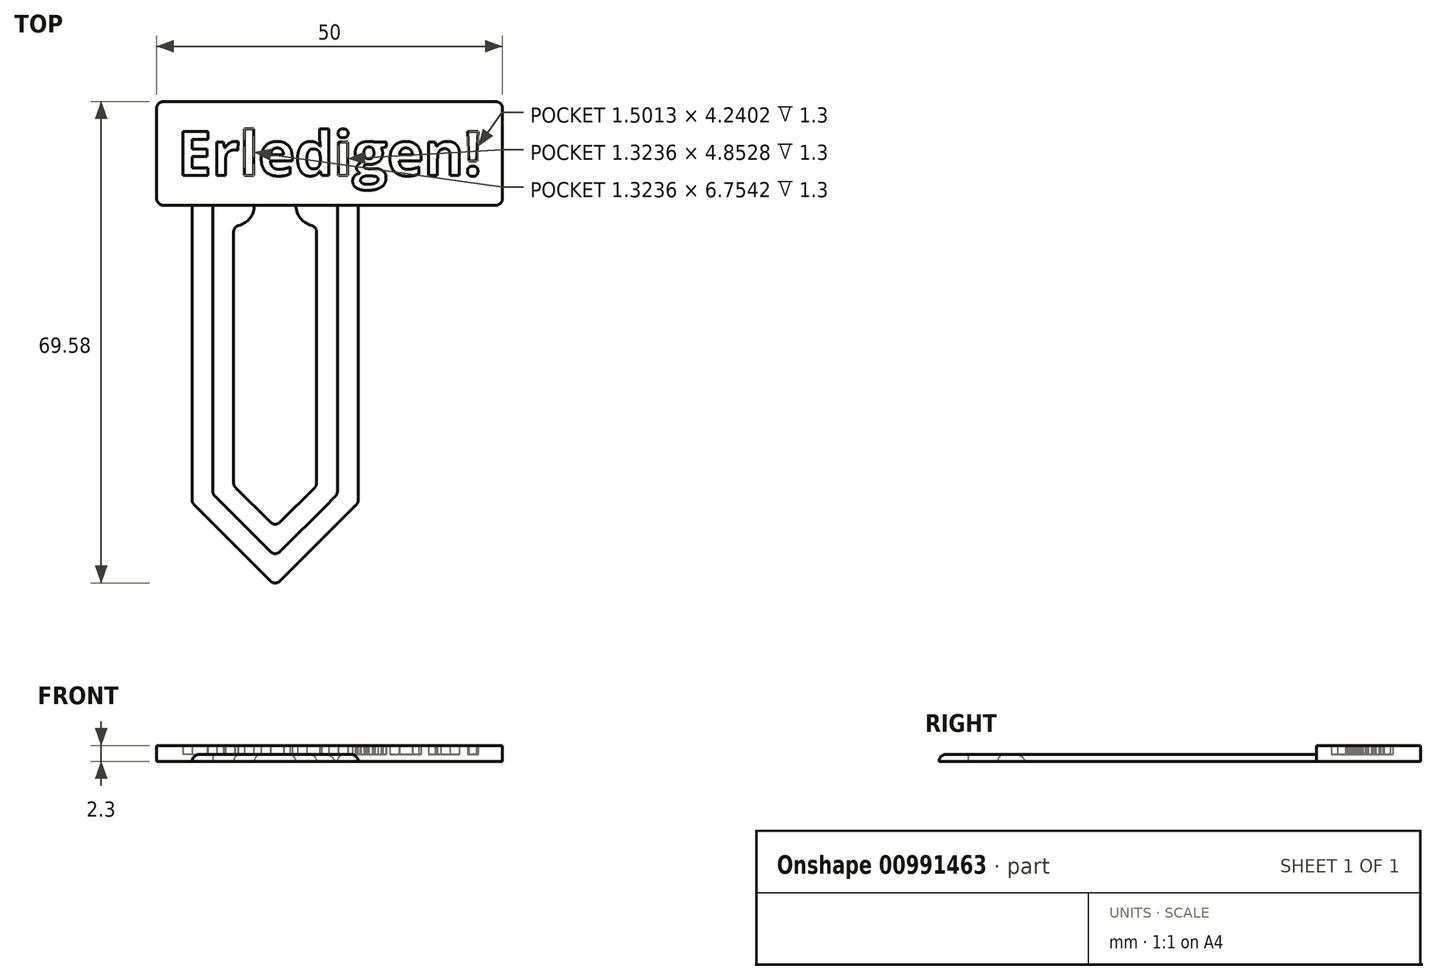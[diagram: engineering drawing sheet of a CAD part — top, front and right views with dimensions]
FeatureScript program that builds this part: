
annotation { "Feature Type Name" : "Feature", "Feature Type Description" : "" }
export const myFeature = defineFeature(function(context is Context, id is Id, definition is map)
    precondition{}
    {
        {
            var Q0;
            Q0=qCreatedBy(makeId("Top.planeOp"),FACE);
            var sketch = newSketch(context, id + "F0", { "sketchPlane" : qUnion([Q0])});
            skLineSegment(sketch, "E0", {"start": v(-14.18, 18.01) * mm, "end": v(-14.18, -24.99) * mm});
            skLineSegment(sketch, "E1", {"start": v(-11.18, 18.01) * mm, "end": v(-11.18, -23.75) * mm});
            skLineSegment(sketch, "E2", {"start": v(-8.18, 15.01) * mm, "end": v(-8.18, -22.5) * mm});
            skLineSegment(sketch, "E3", {"start": v(-2.18, 18.01) * mm, "end": v(-2.18, -9.23) * mm, "construction": true});
            skLineSegment(sketch, "E4", {"start": v(-8.18, -22.5) * mm, "end": v(-2.18, -28.5) * mm});
            skLineSegment(sketch, "E5", {"start": v(-11.18, -23.75) * mm, "end": v(-2.18, -32.75) * mm});
            skLineSegment(sketch, "E6", {"start": v(-2.18, -36.99) * mm, "end": v(-14.18, -24.99) * mm});
            skLineSegment(sketch, "E7.MirrorCS", {"start": v(9.82, 18.01) * mm, "end": v(9.82, -24.99) * mm});
            skLineSegment(sketch, "E8.MirrorCS", {"start": v(6.82, 18.01) * mm, "end": v(6.82, -23.75) * mm});
            skLineSegment(sketch, "E9.MirrorCS", {"start": v(3.82, -22.5) * mm, "end": v(-2.18, -28.5) * mm});
            skLineSegment(sketch, "E10.MirrorCS", {"start": v(6.82, -23.75) * mm, "end": v(-2.18, -32.75) * mm});
            skLineSegment(sketch, "E11.MirrorCS", {"start": v(3.82, 15.01) * mm, "end": v(3.82, -22.5) * mm});
            skLineSegment(sketch, "E12.MirrorCS", {"start": v(-2.18, -36.99) * mm, "end": v(9.82, -24.99) * mm});
            skLineSegment(sketch, "E13.bottom", {"start": v(30.68, 18.01) * mm, "end": v(-19.32, 18.01) * mm});
            skLineSegment(sketch, "E13.top", {"start": v(30.68, 33.01) * mm, "end": v(-19.32, 33.01) * mm});
            skLineSegment(sketch, "E13.left", {"start": v(30.68, 18.01) * mm, "end": v(30.68, 33.01) * mm});
            skLineSegment(sketch, "E13.right", {"start": v(-19.32, 18.01) * mm, "end": v(-19.32, 33.01) * mm});
            skArc(sketch, "E14", {"start": v(-5.18, 18.01) * mm, "mid": v(-6.06, 15.9) * mm, "end": v(-8.18, 15.01) * mm});
            skArc(sketch, "E15", {"start": v(0.82, 18.01) * mm, "mid": v(1.7, 15.9) * mm, "end": v(3.82, 15.01) * mm});
            skText(sketch, "E16", { "text": "Erledigen!", "fontName": "OpenSans-Bold.ttf"});
            skLineSegment(sketch, "E17", {"start": v(5.68, 33.01) * mm, "end": v(5.68, 18.01) * mm, "construction": true});
            skLineSegment(sketch, "E18", {"start": v(-19.32, 25.51) * mm, "end": v(30.68, 25.51) * mm, "construction": true});
            const initialGuessF0  = {"E16": [-0.01632, 0.02231, 1, 0, 0.0064]};
            skSetInitialGuess(sketch, initialGuessF0);
            skSolve(sketch);
        }
        {
            var Q0;
            {var subQ1=sQuery(id+"F0.wireOp",EDGE,"E0");Q0=makeQuery(id+"F0.imprint","IMPRINT",FACE,{"disambiguationData":[TD([[makeQuery(id+"F0.imprint","IMPRINT",EDGE,{"derivedFrom":subQ1}),1.0]])]});}
            var Q1;
            Q1=makeQuery(id+"F0.imprint","IMPRINT",FACE,{"disambiguationData":[TD([[makeQuery(id+"F0.imprint","IMPRINT",EDGE,{"derivedFrom":sQuery(id+"F0.wireOp",EDGE,"E2")}),1.0]])]});
            var Q2;
            Q2=makeQuery(id+"F0.imprint","IMPRINT",FACE,{"disambiguationData":[TD([[makeQuery(id+"F0.imprint","IMPRINT",EDGE,{"derivedFrom":sQuery(id+"F0.wireOp",EDGE,"E16.sketch_text.stroke-0")}),-1.0]])]});
            var Q3;
            Q3=makeQuery(id+"F0.imprint","IMPRINT",FACE,{"disambiguationData":[TD([[makeQuery(id+"F0.imprint","IMPRINT",EDGE,{"derivedFrom":sQuery(id+"F0.wireOp",EDGE,"E16.sketch_text.stroke-12")}),-1.0]])]});
            var Q4;
            Q4=makeQuery(id+"F0.imprint","IMPRINT",FACE,{"disambiguationData":[TD([[makeQuery(id+"F0.imprint","IMPRINT",EDGE,{"derivedFrom":sQuery(id+"F0.wireOp",EDGE,"E16.sketch_text.stroke-25")}),-1.0]])]});
            var Q5;
            Q5=makeQuery(id+"F0.imprint","IMPRINT",FACE,{"disambiguationData":[TD([[makeQuery(id+"F0.imprint","IMPRINT",EDGE,{"derivedFrom":sQuery(id+"F0.wireOp",EDGE,"E16.sketch_text.stroke-29")}),-1.0]])]});
            var Q6;
            Q6=makeQuery(id+"F0.imprint","IMPRINT",FACE,{"disambiguationData":[TD([[makeQuery(id+"F0.imprint","IMPRINT",EDGE,{"derivedFrom":sQuery(id+"F0.wireOp",EDGE,"E16.sketch_text.stroke-49")}),-1.0]])]});
            var Q7;
            Q7=makeQuery(id+"F0.imprint","IMPRINT",FACE,{"disambiguationData":[TD([[makeQuery(id+"F0.imprint","IMPRINT",EDGE,{"derivedFrom":sQuery(id+"F0.wireOp",EDGE,"E16.sketch_text.stroke-77")}),-1.0]])]});
            var Q8;
            Q8=makeQuery(id+"F0.imprint","IMPRINT",FACE,{"disambiguationData":[TD([[makeQuery(id+"F0.imprint","IMPRINT",EDGE,{"derivedFrom":sQuery(id+"F0.wireOp",EDGE,"E16.sketch_text.stroke-72")}),-1.0]])]});
            var Q9;
            Q9=makeQuery(id+"F0.imprint","IMPRINT",FACE,{"disambiguationData":[TD([[makeQuery(id+"F0.imprint","IMPRINT",EDGE,{"derivedFrom":sQuery(id+"F0.wireOp",EDGE,"E16.sketch_text.stroke-81")}),-1.0]])]});
            var Q10;
            Q10=makeQuery(id+"F0.imprint","IMPRINT",FACE,{"disambiguationData":[TD([[makeQuery(id+"F0.imprint","IMPRINT",EDGE,{"derivedFrom":sQuery(id+"F0.wireOp",EDGE,"E16.sketch_text.stroke-125")}),-1.0]])]});
            var Q11;
            Q11=makeQuery(id+"F0.imprint","IMPRINT",FACE,{"disambiguationData":[TD([[makeQuery(id+"F0.imprint","IMPRINT",EDGE,{"derivedFrom":sQuery(id+"F0.wireOp",EDGE,"E16.sketch_text.stroke-145")}),-1.0]])]});
            var Q12;
            Q12=makeQuery(id+"F0.imprint","IMPRINT",FACE,{"disambiguationData":[TD([[makeQuery(id+"F0.imprint","IMPRINT",EDGE,{"derivedFrom":sQuery(id+"F0.wireOp",EDGE,"E16.sketch_text.stroke-162")}),-1.0]])]});
            var Q13;
            Q13=makeQuery(id+"F0.imprint","IMPRINT",FACE,{"disambiguationData":[TD([[makeQuery(id+"F0.imprint","IMPRINT",EDGE,{"derivedFrom":sQuery(id+"F0.wireOp",EDGE,"E16.sketch_text.stroke-166")}),-1.0]])]});
            extrude(context, id + "F1", {"entities" : qUnion([Q0, Q1, Q2, Q3, Q4, Q5, Q6, Q7, Q8, Q9, Q10, Q11, Q12, Q13]), "depth" : 1 * mm, "offsetDistance" : 25 * mm});
        }
        {
            var Q0;
            Q0=makeQuery(id+"F0.imprint","IMPRINT",FACE,{"disambiguationData":[TD([[makeQuery(id+"F0.imprint","IMPRINT",EDGE,{"derivedFrom":sQuery(id+"F0.wireOp",EDGE,"E13.top")}),1.0]])]});
            var Q1;
            Q1=makeQuery(id+"F0.imprint","IMPRINT",FACE,{"disambiguationData":[TD([[makeQuery(id+"F0.imprint","IMPRINT",EDGE,{"derivedFrom":sQuery(id+"F0.wireOp",EDGE,"E16.sketch_text.stroke-63")}),1.0]])]});
            var Q2;
            Q2=makeQuery(id+"F0.imprint","IMPRINT",FACE,{"disambiguationData":[TD([[makeQuery(id+"F0.imprint","IMPRINT",EDGE,{"derivedFrom":sQuery(id+"F0.wireOp",EDGE,"E16.sketch_text.stroke-29")}),1.0]])]});
            var Q3;
            Q3=makeQuery(id+"F0.imprint","IMPRINT",FACE,{"disambiguationData":[TD([[makeQuery(id+"F0.imprint","IMPRINT",EDGE,{"derivedFrom":sQuery(id+"F0.wireOp",EDGE,"E16.sketch_text.stroke-119")}),1.0]])]});
            var Q4;
            Q4=makeQuery(id+"F0.imprint","IMPRINT",FACE,{"disambiguationData":[TD([[makeQuery(id+"F0.imprint","IMPRINT",EDGE,{"derivedFrom":sQuery(id+"F0.wireOp",EDGE,"E16.sketch_text.stroke-110")}),1.0]])]});
            var Q5;
            Q5=makeQuery(id+"F0.imprint","IMPRINT",FACE,{"disambiguationData":[TD([[makeQuery(id+"F0.imprint","IMPRINT",EDGE,{"derivedFrom":sQuery(id+"F0.wireOp",EDGE,"E16.sketch_text.stroke-125")}),1.0]])]});
            extrude(context, id + "F2", {"entities" : qUnion([Q0, Q1, Q2, Q3, Q4, Q5]), "operationType" : NewBodyOperationType.ADD, "depth" : 2.3 * mm, "offsetDistance" : 25 * mm});
        }
        {
            var Q0;
            Q0=makeQuery(id+"F2.opExtrude","SWEPT_EDGE",EDGE,{"disambiguationData":[OSD([sQuery(id+"F0.wireOp",EDGE,"E13.bottom"),sQuery(id+"F0.wireOp",EDGE,"E13.right")])]});
            var Q1;
            Q1=makeQuery(id+"F1.opExtrude","SWEPT_EDGE",EDGE,{"disambiguationData":[OSD([sQuery(id+"F0.wireOp",EDGE,"E2"),sQuery(id+"F0.wireOp",EDGE,"E14")])]});
            var Q2;
            Q2=makeQuery(id+"F2.opExtrude","SWEPT_EDGE",EDGE,{"disambiguationData":[OSD([sQuery(id+"F0.wireOp",EDGE,"E13.top"),sQuery(id+"F0.wireOp",EDGE,"E13.right")])]});
            var Q3;
            Q3=makeQuery(id+"F1.opExtrude","SWEPT_EDGE",EDGE,{"disambiguationData":[OSD([sQuery(id+"F0.wireOp",EDGE,"E0"),sQuery(id+"F0.wireOp",EDGE,"E6")])]});
            var Q4;
            Q4=makeQuery(id+"F1.opExtrude","SWEPT_EDGE",EDGE,{"disambiguationData":[OSD([sQuery(id+"F0.wireOp",EDGE,"E2"),sQuery(id+"F0.wireOp",EDGE,"E4")])]});
            var Q5;
            Q5=makeQuery(id+"F1.opExtrude","SWEPT_EDGE",EDGE,{"disambiguationData":[OSD([sQuery(id+"F0.wireOp",EDGE,"E6"),sQuery(id+"F0.wireOp",EDGE,"E12.MirrorCS")])]});
            var Q6;
            Q6=makeQuery(id+"F1.opExtrude","SWEPT_EDGE",EDGE,{"disambiguationData":[OSD([sQuery(id+"F0.wireOp",EDGE,"E4"),sQuery(id+"F0.wireOp",EDGE,"E9.MirrorCS")])]});
            var Q7;
            Q7=makeQuery(id+"F1.opExtrude","SWEPT_EDGE",EDGE,{"disambiguationData":[OSD([sQuery(id+"F0.wireOp",EDGE,"E9.MirrorCS"),sQuery(id+"F0.wireOp",EDGE,"E11.MirrorCS")])]});
            var Q8;
            Q8=makeQuery(id+"F1.opExtrude","SWEPT_EDGE",EDGE,{"disambiguationData":[OSD([sQuery(id+"F0.wireOp",EDGE,"E1"),sQuery(id+"F0.wireOp",EDGE,"E5")])]});
            var Q9;
            Q9=makeQuery(id+"F1.opExtrude","SWEPT_EDGE",EDGE,{"disambiguationData":[OSD([sQuery(id+"F0.wireOp",EDGE,"E11.MirrorCS"),sQuery(id+"F0.wireOp",EDGE,"E15")])]});
            var Q10;
            Q10=makeQuery(id+"F2.opExtrude","SWEPT_EDGE",EDGE,{"disambiguationData":[OSD([sQuery(id+"F0.wireOp",EDGE,"E13.top"),sQuery(id+"F0.wireOp",EDGE,"E13.left")])]});
            var Q11;
            Q11=makeQuery(id+"F2.opExtrude","SWEPT_EDGE",EDGE,{"disambiguationData":[OSD([sQuery(id+"F0.wireOp",EDGE,"E13.bottom"),sQuery(id+"F0.wireOp",EDGE,"E13.left")])]});
            var Q12;
            Q12=makeQuery(id+"F1.opExtrude","SWEPT_EDGE",EDGE,{"disambiguationData":[OSD([sQuery(id+"F0.wireOp",EDGE,"E7.MirrorCS"),sQuery(id+"F0.wireOp",EDGE,"E12.MirrorCS")])]});
            var Q13;
            Q13=makeQuery(id+"F1.opExtrude","SWEPT_EDGE",EDGE,{"disambiguationData":[OSD([sQuery(id+"F0.wireOp",EDGE,"E5"),sQuery(id+"F0.wireOp",EDGE,"E10.MirrorCS")])]});
            var Q14;
            Q14=makeQuery(id+"F1.opExtrude","SWEPT_EDGE",EDGE,{"disambiguationData":[OSD([sQuery(id+"F0.wireOp",EDGE,"E8.MirrorCS"),sQuery(id+"F0.wireOp",EDGE,"E10.MirrorCS")])]});
            var Q15;
            Q15=makeQuery(id+"F1.opExtrude","CAP_EDGE",EDGE,{"disambiguationData":[OSD([sQuery(id+"F0.wireOp",EDGE,"E0")])],"isStart":false});
            var Q16;
            Q16=makeQuery(id+"F1.opExtrude","CAP_EDGE",EDGE,{"disambiguationData":[OSD([sQuery(id+"F0.wireOp",EDGE,"E6")])],"isStart":false});
            var Q17;
            Q17=makeQuery(id+"F1.opExtrude","CAP_EDGE",EDGE,{"disambiguationData":[OSD([sQuery(id+"F0.wireOp",EDGE,"E12.MirrorCS")])],"isStart":false});
            var Q18;
            Q18=makeQuery(id+"F1.opExtrude","CAP_EDGE",EDGE,{"disambiguationData":[OSD([sQuery(id+"F0.wireOp",EDGE,"E7.MirrorCS")])],"isStart":false});
            var Q19;
            Q19=makeQuery(id+"F1.opExtrude","CAP_EDGE",EDGE,{"disambiguationData":[OSD([sQuery(id+"F0.wireOp",EDGE,"E11.MirrorCS")])],"isStart":false});
            var Q20;
            Q20=makeQuery(id+"F1.opExtrude","CAP_EDGE",EDGE,{"disambiguationData":[OSD([sQuery(id+"F0.wireOp",EDGE,"E15")])],"isStart":false});
            var Q21;
            Q21=makeQuery(id+"F1.opExtrude","CAP_EDGE",EDGE,{"disambiguationData":[OSD([sQuery(id+"F0.wireOp",EDGE,"E9.MirrorCS")])],"isStart":false});
            var Q22;
            Q22=makeQuery(id+"F1.opExtrude","CAP_EDGE",EDGE,{"disambiguationData":[OSD([sQuery(id+"F0.wireOp",EDGE,"E4")])],"isStart":false});
            var Q23;
            Q23=makeQuery(id+"F1.opExtrude","CAP_EDGE",EDGE,{"disambiguationData":[OSD([sQuery(id+"F0.wireOp",EDGE,"E2")])],"isStart":false});
            var Q24;
            Q24=makeQuery(id+"F1.opExtrude","CAP_EDGE",EDGE,{"disambiguationData":[OSD([sQuery(id+"F0.wireOp",EDGE,"E14")])],"isStart":false});
            var Q25;
            Q25=makeQuery(id+"F1.opExtrude","CAP_EDGE",EDGE,{"disambiguationData":[OSD([sQuery(id+"F0.wireOp",EDGE,"E8.MirrorCS")])],"isStart":false});
            fillet(context, id + "F3", {"entities" : qUnion([Q0, Q1, Q2, Q3, Q4, Q5, Q6, Q7, Q8, Q9, Q10, Q11, Q12, Q13, Q14, Q15, Q16, Q17, Q18, Q19, Q20, Q21, Q22, Q23, Q24, Q25]), "radius" : 1 * mm, "tangentPropagation" : true, "allowEdgeOverflow" : false});
        }
    });
